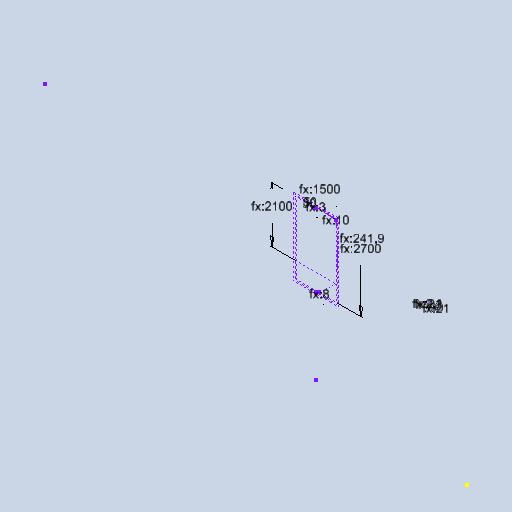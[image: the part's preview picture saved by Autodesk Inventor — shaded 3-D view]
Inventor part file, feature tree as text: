
AUTODESK INVENTOR PART (.ipt)
format: ipt  version: 2025 (Build 290162010, 162A)  size: 304,640 bytes
history: native  units: mm
features: sketch x1
ambient origin geometry x8: Origin, YZ Plane, XZ Plane, XY Plane, X Axis, Y Axis, Z Axis, Center Point
feature tree (1):
  sketch  "Sketch3"  dims[d136=1500.0mm d137=2700.0mm d138=2100.0mm d139=8.0mm d140=50.0mm d141=50.0mm d142=3.0mm d143=10.0mm d144=241.9mm d148=3.0mm d150=5.0mm d194=2.1mm d195=21.0mm d196=21.0mm d197=300.0mm d200=2.0mm d201=30.0mm]
